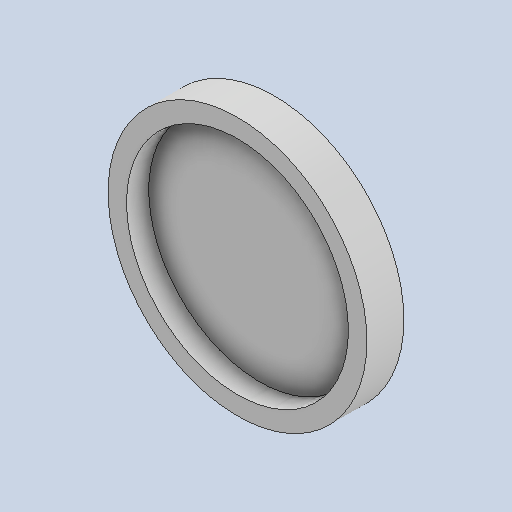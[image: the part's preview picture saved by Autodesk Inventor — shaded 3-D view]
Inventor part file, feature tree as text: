
AUTODESK INVENTOR PART (.ipt)
format: ipt  version: 2025 (Build 290162010, 162A)  size: 121,344 bytes
history: native  units: mm
features: extrude x2
ambient origin geometry x8: Origin, YZ Plane, XZ Plane, XY Plane, X Axis, Y Axis, Z Axis, Center Point
bodies: Solid1 (feature_tree)
feature tree (2):
  extrude  "Extrusion1"  Depth=70.0mm
  extrude  "Extrusion2"  Depth=10.0mm TaperAngle=0.0deg
